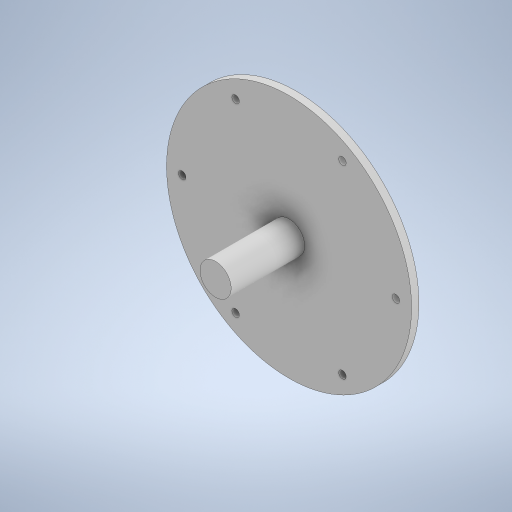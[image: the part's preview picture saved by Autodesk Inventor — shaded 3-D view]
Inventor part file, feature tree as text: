
AUTODESK INVENTOR PART (.ipt)
format: ipt  version: 2024 (Build 280153000, 153)  size: 245,248 bytes
history: native  units: mm
features: extrude x3, sketch x3
ambient origin geometry x8: Origin, YZ Plane, XZ Plane, XY Plane, X Axis, Y Axis, Z Axis, Center Point
bodies: Solid1 (feature_tree)
feature tree (6):
  extrude  "Extrusion1"  Depth=3.0mm TaperAngle=0.0deg
  extrude  "Extrusion2"  Depth=30.0mm TaperAngle=0.0deg
  extrude  "Extrusion3"  Depth=3.0mm TaperAngle=360.0deg
  sketch  "Sketch1"  dims[d0=100.0mm d1=3.0mm d2=0.0mm]
  sketch  "Sketch2"  dims[d3=12.7mm d4=30.0mm d5=0.0mm]
  sketch  "Sketch3"  dims[d6=3.0mm d7=60.0mm d9=360.0deg d11=0.0mm d12=0.0mm]
